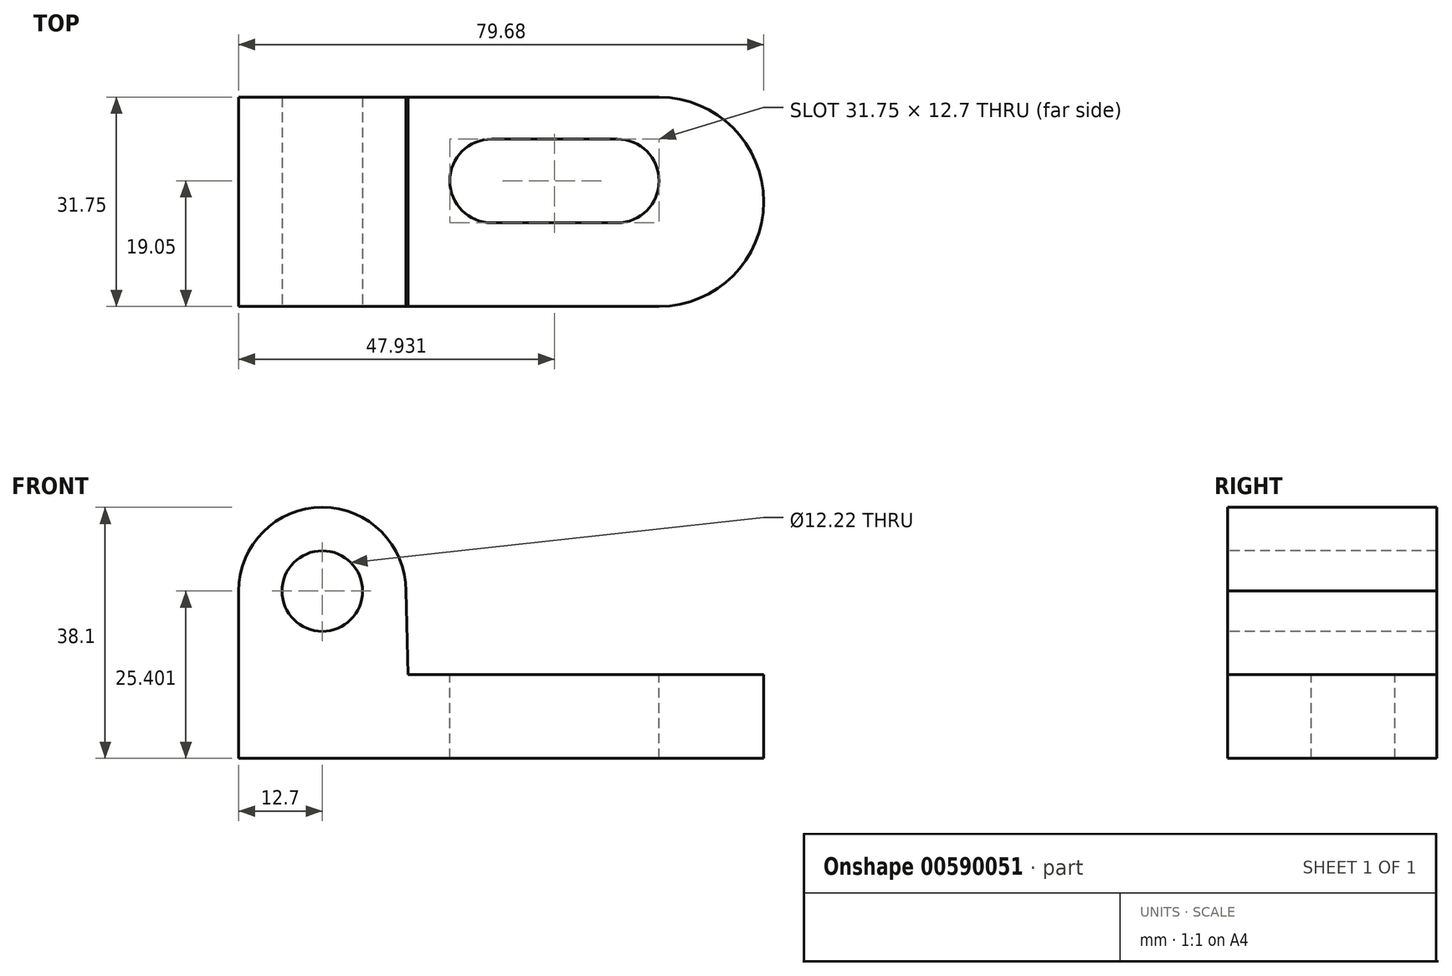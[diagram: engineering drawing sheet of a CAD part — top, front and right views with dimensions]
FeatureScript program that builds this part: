
annotation { "Feature Type Name" : "Feature", "Feature Type Description" : "" }
export const myFeature = defineFeature(function(context is Context, id is Id, definition is map)
    precondition{}
    {
        {
            var Q0;
            Q0=qCreatedBy(makeId("Front.planeOp"),FACE);
            var sketch = newSketch(context, id + "F0", { "sketchPlane" : qUnion([Q0])});
            skLineSegment(sketch, "E0", {"start": v(-67.42, 46.5) * mm, "end": v(-67.42, 21.1) * mm});
            skLineSegment(sketch, "E1", {"start": v(-67.42, 21.1) * mm, "end": v(-3.61, 21.1) * mm});
            skLineSegment(sketch, "E2", {"start": v(-67.42, 46.5) * mm, "end": v(-42.02, 46.5) * mm});
            skLineSegment(sketch, "E3", {"start": v(-3.61, 21.1) * mm, "end": v(-3.61, 33.8) * mm});
            skLineSegment(sketch, "E4", {"start": v(-3.61, 33.8) * mm, "end": v(-41.71, 33.8) * mm});
            skLineSegment(sketch, "E5", {"start": v(-42.02, 46.5) * mm, "end": v(-41.71, 33.8) * mm});
            skSolve(sketch);
        }
        {
            var Q0;
            Q0=makeQuery(id+"F0.imprint","IMPRINT",FACE,{"disambiguationData":[TD([[makeQuery(id+"F0.imprint","IMPRINT",EDGE,{"derivedFrom":sQuery(id+"F0.wireOp",EDGE,"E0")}),1.0]])]});
            extrude(context, id + "F1", {"entities" : qUnion([Q0]), "depth" : 31.75 * mm, "offsetDistance" : 25.4 * mm});
        }
        {
            var Q0;
            Q0=makeQuery(id+"F1.opExtrude","CAP_FACE",FACE,{"disambiguationData":[OSD([sQuery(id+"F0.wireOp",EDGE,"E0"),sQuery(id+"F0.wireOp",EDGE,"E1"),sQuery(id+"F0.wireOp",EDGE,"E2"),sQuery(id+"F0.wireOp",EDGE,"E3"),sQuery(id+"F0.wireOp",EDGE,"E4"),sQuery(id+"F0.wireOp",EDGE,"E5")])],"isStart":false});
            var sketch = newSketch(context, id + "F2", { "sketchPlane" : qUnion([Q0])});
            skPoint(sketch, "E6.endSnap0", {"position": v(-54.72, 46.5) * mm});
            skArc(sketch, "E7", {"start": v(-42.02, 46.5) * mm, "mid": v(-54.72, 59.2) * mm, "end": v(-67.42, 46.5) * mm});
            skSolve(sketch);
        }
        {
            var Q0;
            Q0=makeQuery(id+"F2.imprint","IMPRINT",FACE,{"disambiguationData":[TD([[makeQuery(id+"F2.imprint","IMPRINT",EDGE,{"derivedFrom":sQuery(id+"F2.wireOp",EDGE,"E7")}),1.0]])]});
            extrude(context, id + "F3", {"entities" : qUnion([Q0]), "operationType" : NewBodyOperationType.ADD, "oppositeDirection" : true, "depth" : 31.75 * mm, "offsetDistance" : 25.4 * mm});
        }
        {
            var Q0;
            {var subQ0=sQuery(id+"F0.wireOp",EDGE,"E2");Q0=makeQuery(id+"F3.boolean.opBoolean","MERGE",FACE,{"derivedFrom":[makeQuery(id+"F1.opExtrude","CAP_FACE",FACE,{"disambiguationData":[OSD([sQuery(id+"F0.wireOp",EDGE,"E0"),sQuery(id+"F0.wireOp",EDGE,"E1"),subQ0,sQuery(id+"F0.wireOp",EDGE,"E3"),sQuery(id+"F0.wireOp",EDGE,"E4"),sQuery(id+"F0.wireOp",EDGE,"E5")])],"isStart":false}),makeQuery(id+"F3.opExtrude","CAP_FACE",FACE,{"disambiguationData":[OSD([subQ0,sQuery(id+"F2.wireOp",EDGE,"E7")])],"isStart":true})]});}
            var sketch = newSketch(context, id + "F4", { "sketchPlane" : qUnion([Q0])});
            skCircle(sketch, "E8", {"center": v(-54.72, 46.5) * mm, "radius": 6.11 * mm});
            skSolve(sketch);
        }
        {
            var Q0;
            Q0=makeQuery(id+"F4.imprint","IMPRINT",FACE,{"disambiguationData":[TD([[makeQuery(id+"F4.imprint","IMPRINT",EDGE,{"derivedFrom":sQuery(id+"F4.wireOp",EDGE,"E8")}),1.0]])]});
            extrude(context, id + "F5", {"entities" : qUnion([Q0]), "operationType" : NewBodyOperationType.REMOVE, "oppositeDirection" : true, "depth" : 31.75 * mm, "offsetDistance" : 25.4 * mm});
        }
        {
            var Q0;
            Q0=makeQuery(id+"F1.opExtrude","SWEPT_FACE",FACE,{"disambiguationData":[OSD([sQuery(id+"F0.wireOp",EDGE,"E4")])]});
            var sketch = newSketch(context, id + "F6", { "sketchPlane" : qUnion([Q0])});
            skArc(sketch, "E9", {"start": v(-3.61, -31.75) * mm, "mid": v(12.26, -15.88) * mm, "end": v(-3.61, 0) * mm});
            skSolve(sketch);
        }
        {
            var Q0;
            Q0 = qSketchRegion(id + "F6", true);
            var Q1;
            Q1=makeQuery(id+"F6.imprint","IMPRINT",FACE,{"disambiguationData":[TD([[makeQuery(id+"F6.imprint","IMPRINT",EDGE,{"derivedFrom":sQuery(id+"F6.wireOp",EDGE,"E9")}),1.0]])]});
            extrude(context, id + "F7", {"entities" : qUnion([Q0, Q1]), "operationType" : NewBodyOperationType.ADD, "oppositeDirection" : true, "depth" : 12.7 * mm, "offsetDistance" : 25.4 * mm});
        }
        {
            var Q0;
            {var subQ0=sQuery(id+"F0.wireOp",EDGE,"E4");Q0=makeQuery(id+"F7.boolean.opBoolean","MERGE",FACE,{"derivedFrom":[makeQuery(id+"F1.opExtrude","SWEPT_FACE",FACE,{"disambiguationData":[OSD([subQ0])]}),makeQuery(id+"F7.opExtrude","CAP_FACE",FACE,{"disambiguationData":[OSD([sQuery(id+"F0.wireOp",EDGE,"E3"),subQ0,sQuery(id+"F6.wireOp",EDGE,"E9")])],"isStart":true})]});}
            var sketch = newSketch(context, id + "F8", { "sketchPlane" : qUnion([Q0])});
            skLineSegment(sketch, "E10", {"start": v(-41.71, -31.75) * mm, "end": v(-35.36, -31.75) * mm});
            skLineSegment(sketch, "E11", {"start": v(-29.01, -6.35) * mm, "end": v(-9.96, -6.35) * mm});
            skLineSegment(sketch, "E12", {"start": v(-29.01, -19.05) * mm, "end": v(-9.96, -19.05) * mm});
            skArc(sketch, "E13", {"start": v(-29.01, -6.35) * mm, "mid": v(-35.36, -12.7) * mm, "end": v(-29.01, -19.05) * mm});
            skArc(sketch, "E14", {"start": v(-9.96, -19.05) * mm, "mid": v(-3.61, -12.7) * mm, "end": v(-9.96, -6.35) * mm});
            skSolve(sketch);
        }
        {
            var Q0;
            Q0=makeQuery(id+"F8.imprint","IMPRINT",FACE,{"disambiguationData":[TD([[makeQuery(id+"F8.imprint","IMPRINT",EDGE,{"derivedFrom":sQuery(id+"F8.wireOp",EDGE,"E11")}),-1.0]])]});
            extrude(context, id + "F9", {"entities" : qUnion([Q0]), "operationType" : NewBodyOperationType.REMOVE, "oppositeDirection" : true, "depth" : 25.4 * mm, "offsetDistance" : 25.4 * mm});
        }
    });
